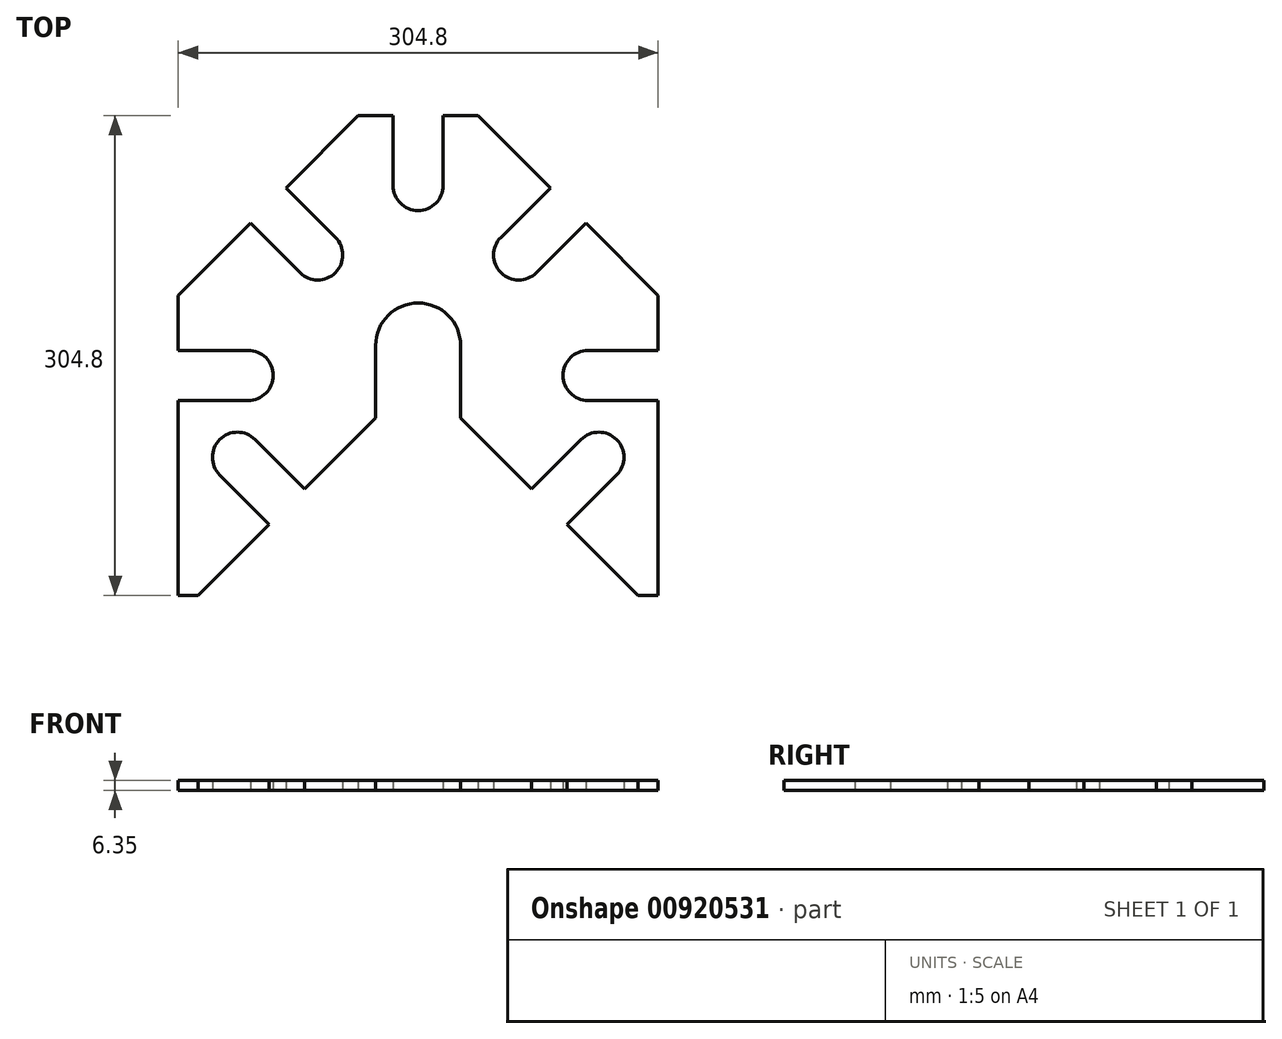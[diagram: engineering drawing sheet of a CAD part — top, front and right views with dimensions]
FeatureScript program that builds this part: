
annotation { "Feature Type Name" : "Feature", "Feature Type Description" : "" }
export const myFeature = defineFeature(function(context is Context, id is Id, definition is map)
    precondition{}
    {
        {
            var Q0;
            Q0=qCreatedBy(makeId("Top.planeOp"),FACE);
            var sketch = newSketch(context, id + "F0", { "sketchPlane" : qUnion([Q0])});
            skLineSegment(sketch, "E0.bottom", {"start": v(-152.4, 0) * mm, "end": v(152.4, 0) * mm});
            skLineSegment(sketch, "E0.top", {"start": v(-152.4, 304.8) * mm, "end": v(152.4, 304.8) * mm});
            skLineSegment(sketch, "E0.left", {"start": v(-152.4, 0) * mm, "end": v(-152.4, 304.8) * mm});
            skLineSegment(sketch, "E0.right", {"start": v(152.4, 0) * mm, "end": v(152.4, 304.8) * mm});
            skLineSegment(sketch, "E1", {"start": v(-152.4, 190.5) * mm, "end": v(-38.1, 304.8) * mm});
            skLineSegment(sketch, "E2", {"start": v(152.4, 190.5) * mm, "end": v(38.1, 304.8) * mm});
            skLineSegment(sketch, "E3", {"start": v(-139.7, 0) * mm, "end": v(-26.99, 112.71) * mm});
            skLineSegment(sketch, "E4", {"start": v(139.7, 0) * mm, "end": v(26.99, 112.71) * mm});
            skArc(sketch, "E5", {"start": v(-15.88, 260.35) * mm, "mid": v(0, 244.48) * mm, "end": v(15.88, 260.35) * mm});
            skLineSegment(sketch, "E6.0", {"start": v(-15.88, 304.8) * mm, "end": v(-15.88, 260.35) * mm});
            skLineSegment(sketch, "E7.0", {"start": v(15.87, 304.8) * mm, "end": v(15.88, 260.35) * mm});
            skArc(sketch, "E8", {"start": v(-75.04, 205) * mm, "mid": v(-52.6, 205) * mm, "end": v(-52.6, 227.44) * mm});
            skLineSegment(sketch, "E9.0", {"start": v(-106.48, 236.42) * mm, "end": v(-75.04, 205) * mm});
            skLineSegment(sketch, "E10.0", {"start": v(-84.02, 258.88) * mm, "end": v(-52.6, 227.44) * mm});
            skLineSegment(sketch, "E11", {"start": v(95.25, 247.65) * mm, "end": v(63.82, 216.22) * mm, "construction": true});
            skCircle(sketch, "E12", {"center": v(63.82, 216.22) * mm, "radius": 15.88 * mm});
            skLineSegment(sketch, "E13.0", {"start": v(84.02, 258.88) * mm, "end": v(52.6, 227.44) * mm});
            skLineSegment(sketch, "E14.0", {"start": v(106.48, 236.42) * mm, "end": v(75.04, 205) * mm});
            skLineSegment(sketch, "E15.0", {"start": v(0, 0) * mm, "end": v(0, 304.8) * mm, "construction": true});
            skLineSegment(sketch, "E16.0", {"start": v(26.99, 112.71) * mm, "end": v(26.99, 158.75) * mm});
            skLineSegment(sketch, "E17.0", {"start": v(-26.99, 112.71) * mm, "end": v(-26.99, 158.75) * mm});
            skLineSegment(sketch, "E18", {"start": v(-83.34, 56.36) * mm, "end": v(-114.77, 87.79) * mm, "construction": true});
            skCircle(sketch, "E19", {"center": v(-114.77, 87.79) * mm, "radius": 15.88 * mm});
            skLineSegment(sketch, "E20.0", {"start": v(-94.57, 45.13) * mm, "end": v(-126, 76.56) * mm});
            skLineSegment(sketch, "E21.0", {"start": v(-72.12, 67.58) * mm, "end": v(-103.55, 99.01) * mm});
            skCircle(sketch, "E22", {"center": v(114.77, 87.79) * mm, "radius": 15.88 * mm});
            skLineSegment(sketch, "E23", {"start": v(83.34, 56.36) * mm, "end": v(114.77, 87.79) * mm, "construction": true});
            skLineSegment(sketch, "E24.0", {"start": v(94.57, 45.13) * mm, "end": v(126, 76.56) * mm});
            skLineSegment(sketch, "E25.0", {"start": v(72.12, 67.58) * mm, "end": v(103.55, 99.01) * mm});
            skArc(sketch, "E26", {"start": v(26.99, 158.75) * mm, "mid": v(0, 185.74) * mm, "end": v(-26.99, 158.75) * mm});
            skLineSegment(sketch, "E27.0", {"start": v(-152.4, 139.7) * mm, "end": v(-107.95, 139.7) * mm, "construction": true});
            skCircle(sketch, "E28", {"center": v(-107.95, 139.7) * mm, "radius": 15.88 * mm});
            skLineSegment(sketch, "E29.0", {"start": v(-152.4, 123.83) * mm, "end": v(-107.95, 123.83) * mm});
            skLineSegment(sketch, "E30.0", {"start": v(-152.4, 155.58) * mm, "end": v(-107.95, 155.58) * mm});
            skCircle(sketch, "E31.MirrorC", {"center": v(107.95, 139.7) * mm, "radius": 15.88 * mm});
            skLineSegment(sketch, "E32.MirrorCS", {"start": v(152.4, 123.83) * mm, "end": v(107.95, 123.83) * mm});
            skLineSegment(sketch, "E33.MirrorCS", {"start": v(152.4, 139.7) * mm, "end": v(107.95, 139.7) * mm, "construction": true});
            skLineSegment(sketch, "E34.MirrorCS", {"start": v(152.4, 155.58) * mm, "end": v(107.95, 155.58) * mm});
            skSolve(sketch);
        }
        {
            var Q0;
            Q0=makeQuery(id+"F0.imprint","IMPRINT",FACE,{"disambiguationData":[TD([[makeQuery(id+"F0.imprint","IMPRINT",EDGE,{"derivedFrom":sQuery(id+"F0.wireOp",EDGE,"E5")}),-1.0]])]});
            extrude(context, id + "F1", {"entities" : qUnion([Q0]), "depth" : 6.35 * mm, "offsetDistance" : 25.4 * mm});
        }
    });
